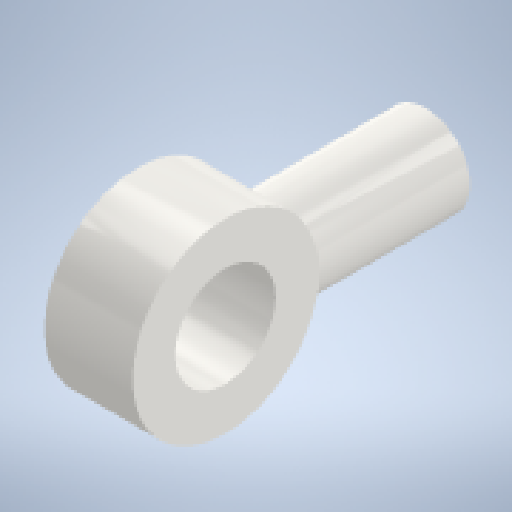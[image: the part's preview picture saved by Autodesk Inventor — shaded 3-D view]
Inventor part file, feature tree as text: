
AUTODESK INVENTOR PART (.ipt)
format: ipt  version: 2024 (Build 280153000, 153)  size: 221,696 bytes
history: native  units: in
note: dims shown in document units (in); Inventor stores cm internally (conversion verified against a paired STEP export)
features: extrude x3, fillet x3, sketch x3, other x1
ambient origin geometry x8: Origin, YZ Plane, XZ Plane, XY Plane, X Axis, Y Axis, Z Axis, Center Point
bodies: Solid1 (feature_tree)
feature tree (10):
  extrude  "Extrusion1"  Depth=1.9685in TaperAngle=0.0deg
  extrude  "Extrusion2"  Depth=2.4094in TaperAngle=0.0deg
  other  "Full Round Fillet1"
  fillet  "Face Fillet1"
  fillet  "Face Fillet2"
  fillet  "Fillet8"  Radius=1.2008in
  extrude  "Extrusion3"  Depth=0.0787in
  sketch  "Sketch1"  dims[d0=1.1417in d1=1.9685in d2=0.0in]
  sketch  "Sketch2"  dims[d3=2.4094in d4=2.4094in d5=0.0in d6=1.2008in]
  sketch  "Sketch3"  dims[d7=1.2008in d15=0.0787in d16=1.2992in d17=2.4094in d18=0.0in d8=0.0in d9=0.0in]
